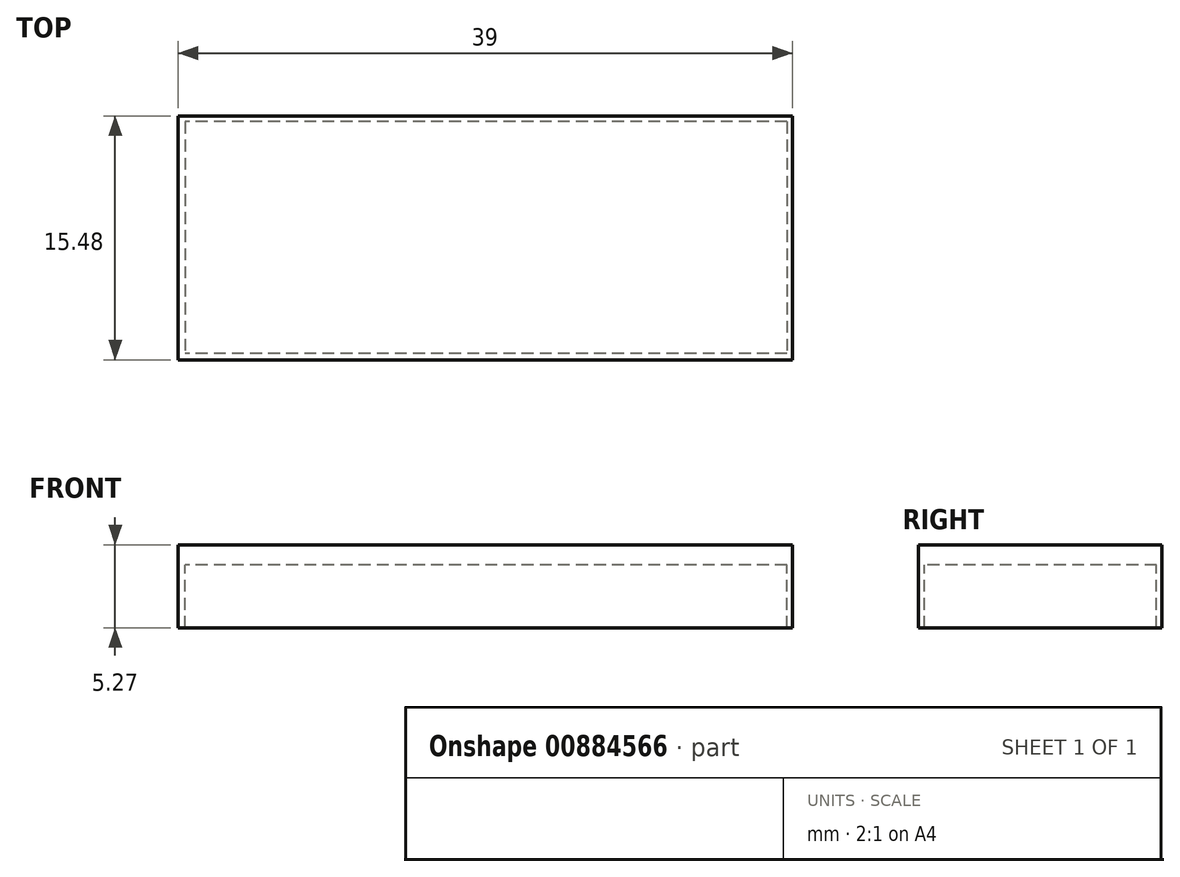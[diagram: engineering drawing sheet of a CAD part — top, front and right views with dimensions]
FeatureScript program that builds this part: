
annotation { "Feature Type Name" : "Feature", "Feature Type Description" : "" }
export const myFeature = defineFeature(function(context is Context, id is Id, definition is map)
    precondition{}
    {
        {
            var Q0;
            Q0=qCreatedBy(makeId("Top.planeOp"),FACE);
            var sketch = newSketch(context, id + "F0", { "sketchPlane" : qUnion([Q0])});
            skLineSegment(sketch, "E0.bottom", {"start": v(-22.8, 12.78) * mm, "end": v(16.2, 12.78) * mm});
            skLineSegment(sketch, "E0.top", {"start": v(-22.8, -2.7) * mm, "end": v(16.2, -2.7) * mm});
            skLineSegment(sketch, "E0.left", {"start": v(-22.8, 12.78) * mm, "end": v(-22.8, -2.7) * mm});
            skLineSegment(sketch, "E0.right", {"start": v(16.2, 12.78) * mm, "end": v(16.2, -2.7) * mm});
            skLineSegment(sketch, "E1", {"start": v(-22.3, 12.3) * mm, "end": v(-22.3, -2.27) * mm});
            skLineSegment(sketch, "E2", {"start": v(-22.3, -2.27) * mm, "end": v(15.61, -2.27) * mm});
            skLineSegment(sketch, "E3", {"start": v(-22.3, 12.3) * mm, "end": v(15.7, 12.3) * mm});
            skLineSegment(sketch, "E4", {"start": v(15.7, 12.3) * mm, "end": v(15.7, -2.27) * mm});
            skSolve(sketch);
        }
        {
            var Q0;
            Q0=makeQuery(id+"F0.imprint","IMPRINT",FACE,{"disambiguationData":[TD([[makeQuery(id+"F0.imprint","IMPRINT",EDGE,{"derivedFrom":sQuery(id+"F0.wireOp",EDGE,"E0.bottom")}),-1.0]])]});
            extrude(context, id + "F1", {"entities" : qUnion([Q0]), "depth" : 1.27 * mm, "offsetDistance" : 25.4 * mm});
        }
        {
            var Q0;
            Q0=makeQuery(id+"F1.opExtrude","CAP_FACE",FACE,{"disambiguationData":[OSD([sQuery(id+"F0.wireOp",EDGE,"E0.bottom"),sQuery(id+"F0.wireOp",EDGE,"E0.top"),sQuery(id+"F0.wireOp",EDGE,"E0.left"),sQuery(id+"F0.wireOp",EDGE,"E0.right")])],"isStart":true});
            var sketch = newSketch(context, id + "F2", { "sketchPlane" : qUnion([Q0])});
            skLineSegment(sketch, "E5.bottom", {"start": v(15.87, -12.43) * mm, "end": v(-22.36, -12.43) * mm});
            skLineSegment(sketch, "E5.top", {"start": v(15.87, 2.3) * mm, "end": v(-22.36, 2.3) * mm});
            skLineSegment(sketch, "E5.left", {"start": v(15.87, -12.43) * mm, "end": v(15.87, 2.3) * mm});
            skLineSegment(sketch, "E5.right", {"start": v(-22.36, -12.43) * mm, "end": v(-22.36, 2.3) * mm});
            skSolve(sketch);
        }
        {
            var Q0;
            Q0=makeQuery(id+"F2.imprint","IMPRINT",FACE,{"disambiguationData":[TD([[makeQuery(id+"F2.imprint","IMPRINT",EDGE,{"derivedFrom":sQuery(id+"F2.wireOp",EDGE,"E5.bottom")}),1.0]])]});
            extrude(context, id + "F3", {"entities" : qUnion([Q0]), "operationType" : NewBodyOperationType.ADD, "depth" : 4 * mm, "offsetDistance" : 25.4 * mm});
        }
    });
